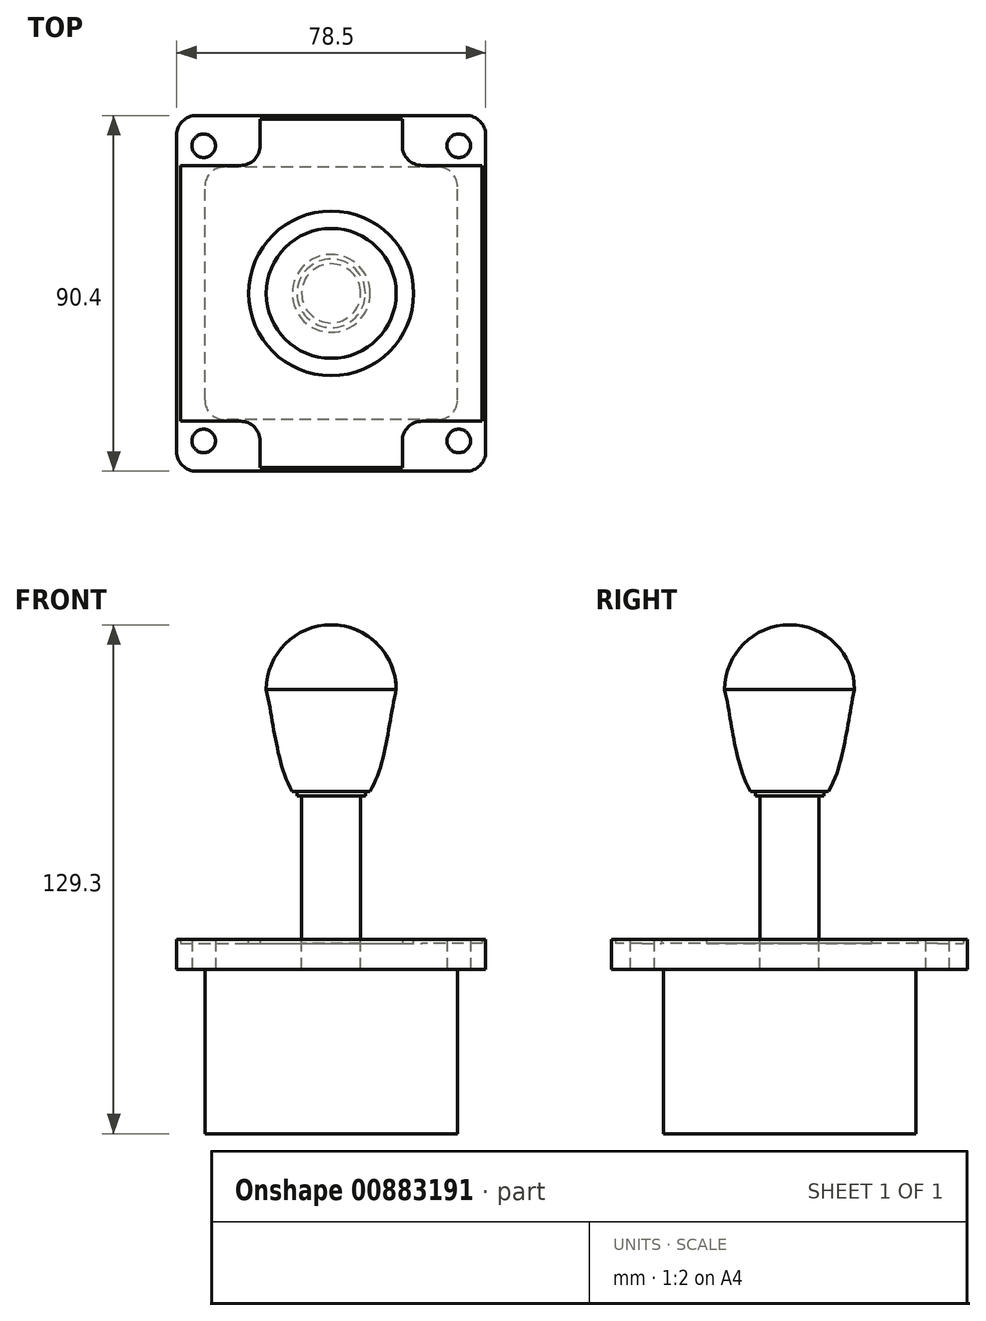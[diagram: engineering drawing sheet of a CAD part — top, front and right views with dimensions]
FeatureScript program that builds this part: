
annotation { "Feature Type Name" : "Feature", "Feature Type Description" : "" }
export const myFeature = defineFeature(function(context is Context, id is Id, definition is map)
    precondition{}
    {
        {
            var Q0;
            Q0=qCreatedBy(makeId("Front.planeOp"),FACE);
            var sketch = newSketch(context, id + "F0", { "sketchPlane" : qUnion([Q0])});
            skLineSegment(sketch, "E0", {"start": v(0, 0) * mm, "end": v(-7.5, 0) * mm});
            skLineSegment(sketch, "E1", {"start": v(-7.5, 0) * mm, "end": v(-7.5, 36.5) * mm});
            skLineSegment(sketch, "E2", {"start": v(-7.5, 36.5) * mm, "end": v(-8.7, 36.5) * mm});
            skLineSegment(sketch, "E3", {"start": v(-8.7, 36.5) * mm, "end": v(-8.7, 37.7) * mm});
            skLineSegment(sketch, "E4", {"start": v(-8.7, 37.7) * mm, "end": v(-9.9, 37.7) * mm});
            skFitSpline(sketch, "E5", {"points": [v(-9.9, 37.7) * mm, v(-16.5, 63.5) * mm], "startDerivative": vector(-12.06, 20.05) * mm, "endDerivative": vector(-5.27, 22.13) * mm});
            skArc(sketch, "E6", {"start": v(0, 80) * mm, "mid": v(-11.67, 75.17) * mm, "end": v(-16.5, 63.5) * mm});
            skLineSegment(sketch, "E7", {"start": v(0, 80) * mm, "end": v(0, 0) * mm});
            skLineSegment(sketch, "E8", {"start": v(0, 119.48) * mm, "end": v(0, 0) * mm, "construction": true});
            skSolve(sketch);
        }
        {
            var Q0;
            Q0=makeQuery(id+"F0.imprint","IMPRINT",FACE,{"disambiguationData":[TD([[makeQuery(id+"F0.imprint","IMPRINT",EDGE,{"derivedFrom":sQuery(id+"F0.wireOp",EDGE,"E0")}),-1.0]])]});
            var Q1;
            Q1=sQuery(id+"F0.wireOp",EDGE,"E8");
            revolve(context, id + "F1", {"surfaceOperationType" : NewSurfaceOperationType.NEW, "entities" : qUnion([Q0]), "axis" : qUnion([Q1]), "revolveType" : RevolveType.FULL});
        }
        {
            var Q0;
            Q0=makeQuery(id+"F1.opRevolve","SWEPT_FACE",FACE,{"disambiguationData":[OSD([sQuery(id+"F0.wireOp",EDGE,"E0")])]});
            var sketch = newSketch(context, id + "F2", { "sketchPlane" : qUnion([Q0])});
            skCircle(sketch, "E9", {"center": v(0, 0) * mm, "radius": 20.93 * mm});
            skSolve(sketch);
        }
        {
            var Q0;
            Q0=makeQuery(id+"F2.imprint","IMPRINT",FACE,{"disambiguationData":[TD([[makeQuery(id+"F2.imprint","IMPRINT",EDGE,{"derivedFrom":sQuery(id+"F2.wireOp",EDGE,"E9")}),1.0]])]});
            extrude(context, id + "F3", {"entities" : qUnion([Q0]), "operationType" : NewBodyOperationType.ADD, "depth" : 1 * mm, "offsetDistance" : 25 * mm});
        }
        {
            var Q0;
            Q0=makeQuery(id+"F3.opExtrude","CAP_FACE",FACE,{"disambiguationData":[OSD([sQuery(id+"F0.wireOp",EDGE,"E0"),sQuery(id+"F0.wireOp",EDGE,"E1"),sQuery(id+"F2.wireOp",EDGE,"E9")])],"isStart":false});
            var sketch = newSketch(context, id + "F4", { "sketchPlane" : qUnion([Q0])});
            skLineSegment(sketch, "E10.bottom", {"start": v(39.25, 45.2) * mm, "end": v(-39.25, 45.2) * mm});
            skLineSegment(sketch, "E10.top", {"start": v(39.25, -45.2) * mm, "end": v(-39.25, -45.2) * mm});
            skLineSegment(sketch, "E10.left", {"start": v(39.25, 45.2) * mm, "end": v(39.25, -45.2) * mm});
            skLineSegment(sketch, "E10.right", {"start": v(-39.25, 45.2) * mm, "end": v(-39.25, -45.2) * mm});
            skPoint(sketch, "E10.middle", {"position": v(0, 0) * mm});
            skSolve(sketch);
        }
        {
            var Q0;
            Q0=makeQuery(id+"F4.imprint","IMPRINT",FACE,{"disambiguationData":[TD([[makeQuery(id+"F4.imprint","IMPRINT",EDGE,{"derivedFrom":sQuery(id+"F4.wireOp",EDGE,"E10.bottom")}),1.0]])]});
            var Q1;
            Q1=makeQuery(id+"F4.imprint","IMPRINT",FACE,{"disambiguationData":[TD([[makeQuery(id+"F4.imprint","IMPRINT",EDGE,{"derivedFrom":makeQuery(id+"F3.opExtrude","CAP_EDGE",EDGE,{"disambiguationData":[OSD([sQuery(id+"F2.wireOp",EDGE,"E9")])],"isStart":false})}),1.0]])]});
            extrude(context, id + "F5", {"entities" : qUnion([Q0, Q1]), "depth" : 6.6 * mm, "offsetDistance" : 25 * mm});
        }
        {
            var Q0;
            Q0=makeQuery(id+"F5.opExtrude","CAP_FACE",FACE,{"disambiguationData":[OSD([sQuery(id+"F0.wireOp",EDGE,"E0"),sQuery(id+"F0.wireOp",EDGE,"E1"),sQuery(id+"F4.wireOp",EDGE,"E10.bottom"),sQuery(id+"F4.wireOp",EDGE,"E10.top"),sQuery(id+"F4.wireOp",EDGE,"E10.left"),sQuery(id+"F4.wireOp",EDGE,"E10.right")])],"isStart":false});
            var sketch = newSketch(context, id + "F6", { "sketchPlane" : qUnion([Q0])});
            skLineSegment(sketch, "E11.bottom", {"start": v(32.1, 32.1) * mm, "end": v(-32.1, 32.1) * mm});
            skLineSegment(sketch, "E11.top", {"start": v(32.1, -32.1) * mm, "end": v(-32.1, -32.1) * mm});
            skLineSegment(sketch, "E11.left", {"start": v(32.1, 32.1) * mm, "end": v(32.1, -32.1) * mm});
            skLineSegment(sketch, "E11.right", {"start": v(-32.1, 32.1) * mm, "end": v(-32.1, -32.1) * mm});
            skPoint(sketch, "E11.middle", {"position": v(0, 0) * mm});
            skSolve(sketch);
        }
        {
            var Q0;
            Q0 = qSketchRegion(id + "F6", true);
            extrude(context, id + "F7", {"entities" : qUnion([Q0]), "operationType" : NewBodyOperationType.ADD, "depth" : 41.7 * mm, "offsetDistance" : 25 * mm});
        }
        {
            var Q0;
            Q0=makeQuery(id+"F5.opExtrude","CAP_FACE",FACE,{"disambiguationData":[OSD([sQuery(id+"F0.wireOp",EDGE,"E0"),sQuery(id+"F0.wireOp",EDGE,"E1"),sQuery(id+"F4.wireOp",EDGE,"E10.bottom"),sQuery(id+"F4.wireOp",EDGE,"E10.top"),sQuery(id+"F4.wireOp",EDGE,"E10.left"),sQuery(id+"F4.wireOp",EDGE,"E10.right")])],"isStart":true});
            var sketch = newSketch(context, id + "F8", { "sketchPlane" : qUnion([Q0])});
            skCircle(sketch, "E12", {"center": v(-32.4, 37.5) * mm, "radius": 3 * mm});
            skLineSegment(sketch, "E13", {"start": v(-39.25, 32.5) * mm, "end": v(-23.07, 32.5) * mm});
            skLineSegment(sketch, "E14", {"start": v(-18.07, 37.5) * mm, "end": v(-18.07, 45.2) * mm});
            skArc(sketch, "E15", {"start": v(-18.07, 37.5) * mm, "mid": v(-19.53, 33.96) * mm, "end": v(-23.07, 32.5) * mm});
            skLineSegment(sketch, "E16.MirrorCS", {"start": v(18.07, 37.5) * mm, "end": v(18.07, 45.2) * mm});
            skArc(sketch, "E17.MirrorCS", {"start": v(18.07, 37.5) * mm, "mid": v(19.53, 33.96) * mm, "end": v(23.07, 32.5) * mm});
            skLineSegment(sketch, "E18.MirrorCS", {"start": v(39.25, 32.5) * mm, "end": v(23.07, 32.5) * mm});
            skCircle(sketch, "E19.MirrorC", {"center": v(32.4, 37.5) * mm, "radius": 3 * mm});
            skLineSegment(sketch, "E20", {"start": v(-18.07, 44.2) * mm, "end": v(18.07, 44.2) * mm});
            skLineSegment(sketch, "E21", {"start": v(-38.25, 32.5) * mm, "end": v(-38.25, 0) * mm});
            skLineSegment(sketch, "E22", {"start": v(38.25, 32.5) * mm, "end": v(38.25, 0) * mm});
            skLineSegment(sketch, "E23", {"start": v(-38.25, 0) * mm, "end": v(-39.25, 0) * mm});
            skLineSegment(sketch, "E24", {"start": v(38.25, 0) * mm, "end": v(39.25, 0) * mm});
            skSolve(sketch);
        }
        {
            var Q0;
            Q0=makeQuery(id+"F8.imprint","IMPRINT",FACE,{"disambiguationData":[TD([[makeQuery(id+"F8.imprint","IMPRINT",EDGE,{"derivedFrom":sQuery(id+"F8.wireOp",EDGE,"E12")}),-1.0]])]});
            var Q1;
            {var subQ1=sQuery(id+"F8.wireOp",EDGE,"E16.MirrorCS");Q1=makeQuery(id+"F8.imprint","IMPRINT",FACE,{"disambiguationData":[TD([[makeQuery(id+"F8.imprint","IMPRINT",EDGE,{"derivedFrom":subQ1}),-1.0]])]});}
            var Q2;
            {var subQ3=sQuery(id+"F8.wireOp",EDGE,"E20");Q2=makeQuery(id+"F8.imprint","IMPRINT",FACE,{"disambiguationData":[TD([[makeQuery(id+"F8.imprint","IMPRINT",EDGE,{"derivedFrom":subQ3}),1.0]])]});}
            var Q3;
            {var subQ3=sQuery(id+"F8.wireOp",EDGE,"E21");Q3=makeQuery(id+"F8.imprint","IMPRINT",FACE,{"disambiguationData":[TD([[makeQuery(id+"F8.imprint","IMPRINT",EDGE,{"derivedFrom":subQ3}),-1.0]])]});}
            var Q4;
            {var subQ3=sQuery(id+"F8.wireOp",EDGE,"E22");Q4=makeQuery(id+"F8.imprint","IMPRINT",FACE,{"disambiguationData":[TD([[makeQuery(id+"F8.imprint","IMPRINT",EDGE,{"derivedFrom":subQ3}),1.0]])]});}
            extrude(context, id + "F9", {"entities" : qUnion([Q0, Q1, Q2, Q3, Q4]), "depth" : 1 * mm, "offsetDistance" : 25 * mm});
        }
        {
            var Q0;
            Q0=makeQuery(id+"F9.opExtrude","SWEPT_BODY",BODY,{"disambiguationData":[OSD([sQuery(id+"F4.wireOp",EDGE,"E10.top"),sQuery(id+"F4.wireOp",EDGE,"E10.right"),sQuery(id+"F8.wireOp",EDGE,"E12"),sQuery(id+"F8.wireOp",EDGE,"E13"),sQuery(id+"F8.wireOp",EDGE,"E14"),sQuery(id+"F8.wireOp",EDGE,"E15")])]});
            var Q1;
            Q1=makeQuery(id+"F9.opExtrude","SWEPT_BODY",BODY,{"disambiguationData":[OSD([sQuery(id+"F4.wireOp",EDGE,"E10.top"),sQuery(id+"F4.wireOp",EDGE,"E10.left"),sQuery(id+"F8.wireOp",EDGE,"E16.MirrorCS"),sQuery(id+"F8.wireOp",EDGE,"E17.MirrorCS"),sQuery(id+"F8.wireOp",EDGE,"E18.MirrorCS"),sQuery(id+"F8.wireOp",EDGE,"E19.MirrorC")])]});
            var Q2;
            Q2=qCreatedBy(makeId("Front.planeOp"),FACE);
            mirror(context, id + "F10", {"operationType" : NewBodyOperationType.ADD, "entities" : qUnion([Q0, Q1]), "mirrorPlane" : qUnion([Q2])});
        }
        {
            var Q0;
            Q0=makeQuery(id+"F10.boolean.opBoolean","SPLIT",FACE,{"disambiguationData":[TD([makeQuery(id+"F9.opExtrude","SWEPT_FACE",FACE,{"disambiguationData":[OSD([sQuery(id+"F8.wireOp",EDGE,"E12")])]})])],"derivedFrom":makeQuery(id+"F5.opExtrude","CAP_FACE",FACE,{"disambiguationData":[OSD([sQuery(id+"F0.wireOp",EDGE,"E0"),sQuery(id+"F0.wireOp",EDGE,"E1"),sQuery(id+"F4.wireOp",EDGE,"E10.bottom"),sQuery(id+"F4.wireOp",EDGE,"E10.top"),sQuery(id+"F4.wireOp",EDGE,"E10.left"),sQuery(id+"F4.wireOp",EDGE,"E10.right")])],"isStart":true})});
            var Q1;
            Q1=makeQuery(id+"F10.boolean.opBoolean","SPLIT",FACE,{"disambiguationData":[TD([makeQuery(id+"F9.opExtrude","SWEPT_FACE",FACE,{"disambiguationData":[OSD([sQuery(id+"F8.wireOp",EDGE,"E19.MirrorC")])]})])],"derivedFrom":makeQuery(id+"F5.opExtrude","CAP_FACE",FACE,{"disambiguationData":[OSD([sQuery(id+"F0.wireOp",EDGE,"E0"),sQuery(id+"F0.wireOp",EDGE,"E1"),sQuery(id+"F4.wireOp",EDGE,"E10.bottom"),sQuery(id+"F4.wireOp",EDGE,"E10.top"),sQuery(id+"F4.wireOp",EDGE,"E10.left"),sQuery(id+"F4.wireOp",EDGE,"E10.right")])],"isStart":true})});
            var Q2;
            Q2=makeQuery(id+"F10.boolean.opBoolean","SPLIT",FACE,{"disambiguationData":[TD([makeQuery(id+"F10.opPattern","COPY",FACE,{"derivedFrom":makeQuery(id+"F9.opExtrude","SWEPT_FACE",FACE,{"disambiguationData":[OSD([sQuery(id+"F8.wireOp",EDGE,"E12")])]}),"instanceName":"1"})])],"derivedFrom":makeQuery(id+"F5.opExtrude","CAP_FACE",FACE,{"disambiguationData":[OSD([sQuery(id+"F0.wireOp",EDGE,"E0"),sQuery(id+"F0.wireOp",EDGE,"E1"),sQuery(id+"F4.wireOp",EDGE,"E10.bottom"),sQuery(id+"F4.wireOp",EDGE,"E10.top"),sQuery(id+"F4.wireOp",EDGE,"E10.left"),sQuery(id+"F4.wireOp",EDGE,"E10.right")])],"isStart":true})});
            var Q3;
            Q3=makeQuery(id+"F10.boolean.opBoolean","SPLIT",FACE,{"disambiguationData":[TD([makeQuery(id+"F10.opPattern","COPY",FACE,{"derivedFrom":makeQuery(id+"F9.opExtrude","SWEPT_FACE",FACE,{"disambiguationData":[OSD([sQuery(id+"F8.wireOp",EDGE,"E19.MirrorC")])]}),"instanceName":"1"})])],"derivedFrom":makeQuery(id+"F5.opExtrude","CAP_FACE",FACE,{"disambiguationData":[OSD([sQuery(id+"F0.wireOp",EDGE,"E0"),sQuery(id+"F0.wireOp",EDGE,"E1"),sQuery(id+"F4.wireOp",EDGE,"E10.bottom"),sQuery(id+"F4.wireOp",EDGE,"E10.top"),sQuery(id+"F4.wireOp",EDGE,"E10.left"),sQuery(id+"F4.wireOp",EDGE,"E10.right")])],"isStart":true})});
            extrude(context, id + "F11", {"entities" : qUnion([Q0, Q1, Q2, Q3]), "operationType" : NewBodyOperationType.REMOVE, "endBound" : BoundingType.UP_TO_NEXT, "oppositeDirection" : true, "depth" : 25 * mm, "offsetDistance" : 25 * mm});
        }
        {
            var Q0;
            {var subQ0=sQuery(id+"F4.wireOp",EDGE,"E10.right");Q0=makeQuery(id+"F10.boolean.opBoolean","MERGE",EDGE,{"derivedFrom":[makeQuery(id+"F5.opExtrude","SWEPT_EDGE",EDGE,{"disambiguationData":[OSD([sQuery(id+"F4.wireOp",EDGE,"E10.bottom"),subQ0])]}),makeQuery(id+"F10.opPattern","COPY",EDGE,{"derivedFrom":makeQuery(id+"F9.opExtrude","SWEPT_EDGE",EDGE,{"disambiguationData":[OSD([sQuery(id+"F4.wireOp",EDGE,"E10.top"),subQ0])]}),"instanceName":"1"})]});}
            var Q1;
            {var subQ0=sQuery(id+"F4.wireOp",EDGE,"E10.left");Q1=makeQuery(id+"F10.boolean.opBoolean","MERGE",EDGE,{"derivedFrom":[makeQuery(id+"F5.opExtrude","SWEPT_EDGE",EDGE,{"disambiguationData":[OSD([sQuery(id+"F4.wireOp",EDGE,"E10.bottom"),subQ0])]}),makeQuery(id+"F10.opPattern","COPY",EDGE,{"derivedFrom":makeQuery(id+"F9.opExtrude","SWEPT_EDGE",EDGE,{"disambiguationData":[OSD([sQuery(id+"F4.wireOp",EDGE,"E10.top"),subQ0])]}),"instanceName":"1"})]});}
            var Q2;
            {var subQ0=sQuery(id+"F4.wireOp",EDGE,"E10.left");var subQ1=sQuery(id+"F4.wireOp",EDGE,"E10.top");Q2=makeQuery(id+"F10.boolean.opBoolean","MERGE",EDGE,{"derivedFrom":[makeQuery(id+"F5.opExtrude","SWEPT_EDGE",EDGE,{"disambiguationData":[OSD([subQ1,subQ0])]}),makeQuery(id+"F9.opExtrude","SWEPT_EDGE",EDGE,{"disambiguationData":[OSD([subQ1,subQ0])]})]});}
            var Q3;
            {var subQ0=sQuery(id+"F4.wireOp",EDGE,"E10.right");var subQ1=sQuery(id+"F4.wireOp",EDGE,"E10.top");Q3=makeQuery(id+"F10.boolean.opBoolean","MERGE",EDGE,{"derivedFrom":[makeQuery(id+"F5.opExtrude","SWEPT_EDGE",EDGE,{"disambiguationData":[OSD([subQ1,subQ0])]}),makeQuery(id+"F9.opExtrude","SWEPT_EDGE",EDGE,{"disambiguationData":[OSD([subQ1,subQ0])]})]});}
            var Q4;
            Q4=makeQuery(id+"F7.opExtrude","SWEPT_EDGE",EDGE,{"disambiguationData":[OSD([sQuery(id+"F6.wireOp",EDGE,"E11.bottom"),sQuery(id+"F6.wireOp",EDGE,"E11.right")])]});
            var Q5;
            Q5=makeQuery(id+"F7.opExtrude","SWEPT_EDGE",EDGE,{"disambiguationData":[OSD([sQuery(id+"F6.wireOp",EDGE,"E11.top"),sQuery(id+"F6.wireOp",EDGE,"E11.right")])]});
            var Q6;
            Q6=makeQuery(id+"F7.opExtrude","SWEPT_EDGE",EDGE,{"disambiguationData":[OSD([sQuery(id+"F6.wireOp",EDGE,"E11.bottom"),sQuery(id+"F6.wireOp",EDGE,"E11.left")])]});
            var Q7;
            Q7=makeQuery(id+"F7.opExtrude","SWEPT_EDGE",EDGE,{"disambiguationData":[OSD([sQuery(id+"F6.wireOp",EDGE,"E11.top"),sQuery(id+"F6.wireOp",EDGE,"E11.left")])]});
            fillet(context, id + "F12", {"entities" : qUnion([Q0, Q1, Q2, Q3, Q4, Q5, Q6, Q7]), "radius" : 5 * mm, "tangentPropagation" : true, "allowEdgeOverflow" : false});
        }
    });
